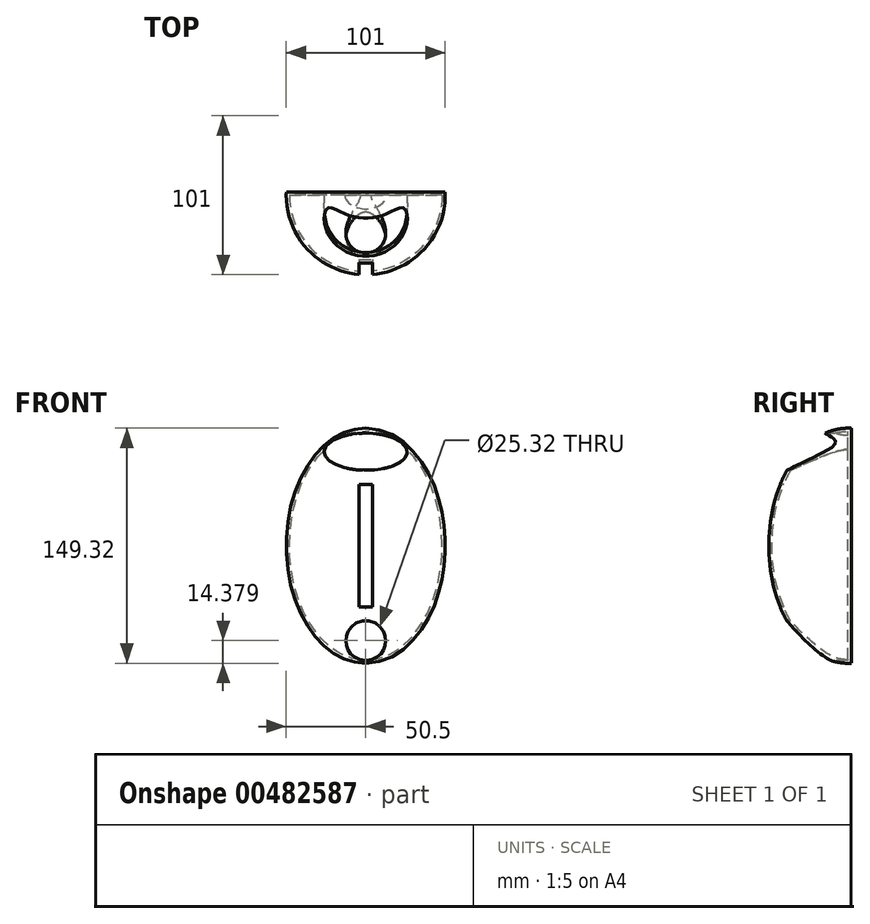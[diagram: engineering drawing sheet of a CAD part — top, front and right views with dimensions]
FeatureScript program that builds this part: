
annotation { "Feature Type Name" : "Feature", "Feature Type Description" : "" }
export const myFeature = defineFeature(function(context is Context, id is Id, definition is map)
    precondition{}
    {
        {
            var Q0;
            Q0=qCreatedBy(makeId("Front.planeOp"),FACE);
            var sketch = newSketch(context, id + "F0", { "sketchPlane" : qUnion([Q0])});
            skEllipticalArc(sketch, "E0", {});
            skLineSegment(sketch, "E1", {"start": v(0, 72.66) * mm, "end": v(0, -72.66) * mm});
            const initialGuessF0  = {"E0": [0, 0, 0, 1, 0.07266349345445633, 0.048504095370168095, 3.141592653589793, 0]};
            skSetInitialGuess(sketch, initialGuessF0);
            skSolve(sketch);
        }
        {
            var Q0;
            Q0=makeQuery(id+"F0.imprint","IMPRINT",FACE,{"disambiguationData":[TD([[makeQuery(id+"F0.imprint","IMPRINT",EDGE,{"derivedFrom":sQuery(id+"F0.wireOp",EDGE,"E0")}),1.0]])]});
            var Q1;
            Q1=sQuery(id+"F0.wireOp",EDGE,"E1");
            revolve(context, id + "F1", {"entities" : qUnion([Q0]), "axis" : qUnion([Q1]), "revolveType" : RevolveType.ONE_DIRECTION, "angle" : 180 * degree});
        }
        {
            var Q0;
            Q0=makeQuery(id+"F1.opRevolve","SWEPT_FACE",FACE,{"disambiguationData":[OSD([sQuery(id+"F0.wireOp",EDGE,"E0")])]});
            var Q1;
            Q1=makeQuery(id+"F1.opRevolve","SWEPT_BODY",BODY,{"disambiguationData":[OSD([sQuery(id+"F0.wireOp",EDGE,"E0"),sQuery(id+"F0.wireOp",EDGE,"E1")])]});
            shell(context, id + "F2", {"isHollow" : true, "entities" : qUnion([Q0]), "parts" : qUnion([Q1]), "thickness" : 2 * mm, "oppositeDirection" : true});
        }
        {
            var Q0;
            Q0=qCreatedBy(makeId("Front.planeOp"),FACE);
            var sketch = newSketch(context, id + "F3", { "sketchPlane" : qUnion([Q0])});
            skLineSegment(sketch, "E2.bottom", {"start": v(-4.2, 38.88) * mm, "end": v(4.2, 38.88) * mm});
            skLineSegment(sketch, "E2.top", {"start": v(-4.2, -38.88) * mm, "end": v(4.2, -38.88) * mm});
            skLineSegment(sketch, "E2.left", {"start": v(-4.2, 38.88) * mm, "end": v(-4.2, -38.88) * mm});
            skLineSegment(sketch, "E2.right", {"start": v(4.2, 38.88) * mm, "end": v(4.2, -38.88) * mm});
            skPoint(sketch, "E2.middle", {"position": v(0, 0) * mm});
            skEllipse(sketch, "E3", {"center": v(0, 59.72) * mm, "majorRadius": 26.42 * mm, "minorRadius": 11.77 * mm, "majorAxis": v(-1, 0)});
            skCircle(sketch, "E4", {"center": v(0, -60.28) * mm, "radius": 12.66 * mm});
            skSolve(sketch);
        }
        {
            var Q0;
            Q0 = qSketchRegion(id + "F3", true);
            extrude(context, id + "F4", {"entities" : qUnion([Q0]), "oppositeDirection" : true, "depth" : 60 * mm});
        }
        {
            var Q0;
            Q0=makeQuery(id+"F4.opExtrude","SWEPT_BODY",BODY,{"disambiguationData":[OSD([sQuery(id+"F3.wireOp",EDGE,"E3")])]});
            var Q1;
            Q1=makeQuery(id+"F4.opExtrude","SWEPT_BODY",BODY,{"disambiguationData":[OSD([sQuery(id+"F3.wireOp",EDGE,"E2.bottom"),sQuery(id+"F3.wireOp",EDGE,"E2.top"),sQuery(id+"F3.wireOp",EDGE,"E2.left"),sQuery(id+"F3.wireOp",EDGE,"E2.right")])]});
            var Q2;
            Q2=makeQuery(id+"F4.opExtrude","SWEPT_BODY",BODY,{"disambiguationData":[OSD([sQuery(id+"F3.wireOp",EDGE,"E4")])]});
            var Q3;
            Q3=qCreatedBy(makeId("Front.planeOp"),FACE);
            transform(context, id + "F5", {"entities" : qUnion([Q0, Q1, Q2]), "transformType" : TransformType.TRANSLATION_DISTANCE, "transformDirection" : qUnion([Q3]), "distance" : 60 * mm, "makeCopy" : false});
        }
        {
            var Q0;
            Q0=makeQuery(id+"F4.opExtrude","SWEPT_BODY",BODY,{"disambiguationData":[OSD([sQuery(id+"F3.wireOp",EDGE,"E3")])]});
            var Q1;
            Q1=makeQuery(id+"F4.opExtrude","SWEPT_BODY",BODY,{"disambiguationData":[OSD([sQuery(id+"F3.wireOp",EDGE,"E2.bottom"),sQuery(id+"F3.wireOp",EDGE,"E2.top"),sQuery(id+"F3.wireOp",EDGE,"E2.left"),sQuery(id+"F3.wireOp",EDGE,"E2.right")])]});
            var Q2;
            Q2=makeQuery(id+"F4.opExtrude","SWEPT_BODY",BODY,{"disambiguationData":[OSD([sQuery(id+"F3.wireOp",EDGE,"E4")])]});
            var Q3;
            Q3=makeQuery(id+"F1.opRevolve","SWEPT_BODY",BODY,{"disambiguationData":[OSD([sQuery(id+"F0.wireOp",EDGE,"E0"),sQuery(id+"F0.wireOp",EDGE,"E1")])]});
            booleanBodies(context, id + "F6", {"operationType" : BooleanOperationType.SUBTRACTION, "tools" : qUnion([Q0, Q1, Q2]), "targets" : qUnion([Q3])});
        }
    });
